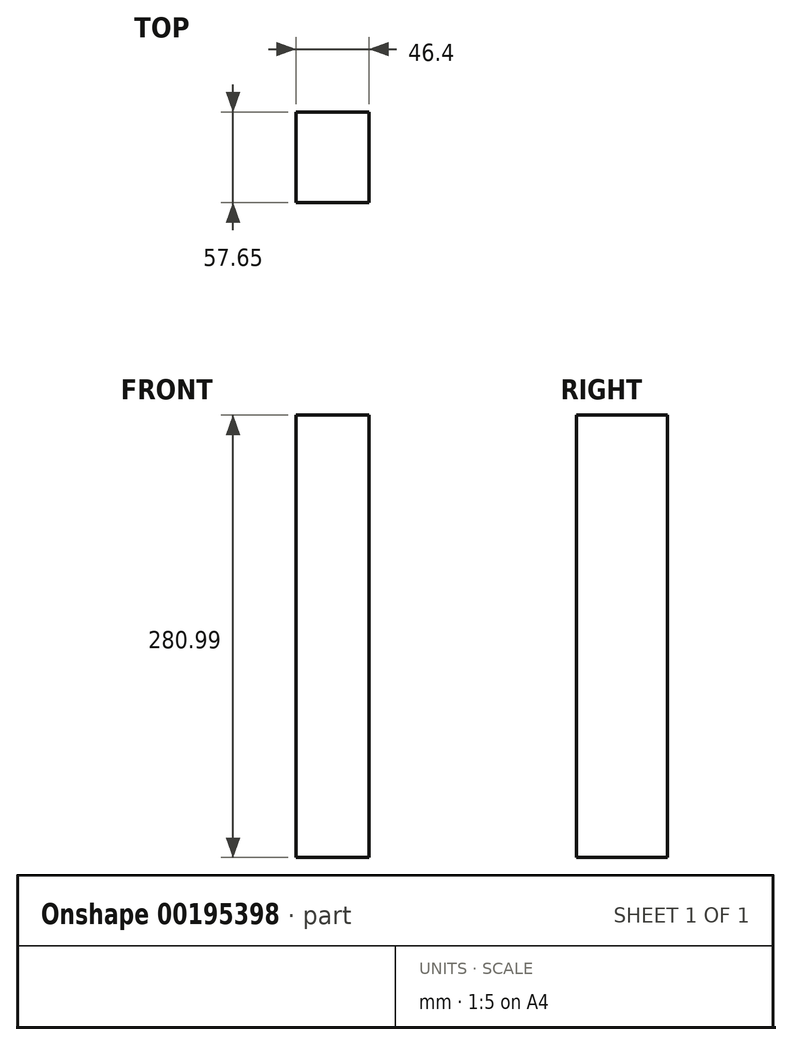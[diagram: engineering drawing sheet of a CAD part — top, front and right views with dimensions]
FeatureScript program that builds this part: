
annotation { "Feature Type Name" : "Feature", "Feature Type Description" : "" }
export const myFeature = defineFeature(function(context is Context, id is Id, definition is map)
    precondition{}
    {
        {
            var Q0;
            Q0=qCreatedBy(makeId("Top.planeOp"),FACE);
            var sketch = newSketch(context, id + "F0", { "sketchPlane" : qUnion([Q0])});
            skLineSegment(sketch, "E0.bottom", {"start": v(0, 0) * mm, "end": v(-46.4, 0) * mm});
            skLineSegment(sketch, "E0.top", {"start": v(0, 57.65) * mm, "end": v(-46.4, 57.65) * mm});
            skLineSegment(sketch, "E0.left", {"start": v(0, 0) * mm, "end": v(0, 57.65) * mm});
            skLineSegment(sketch, "E0.right", {"start": v(-46.4, 0) * mm, "end": v(-46.4, 57.65) * mm});
            skSolve(sketch);
        }
        {
            var Q0;
            Q0=makeQuery(id+"F0.imprint","IMPRINT",FACE,{"disambiguationData":[TD([[makeQuery(id+"F0.imprint","IMPRINT",EDGE,{"derivedFrom":sQuery(id+"F0.wireOp",EDGE,"E0.bottom")}),-1.0]])]});
            extrude(context, id + "F1", {"entities" : qUnion([Q0]), "depth" : 281 * mm});
        }
    });
